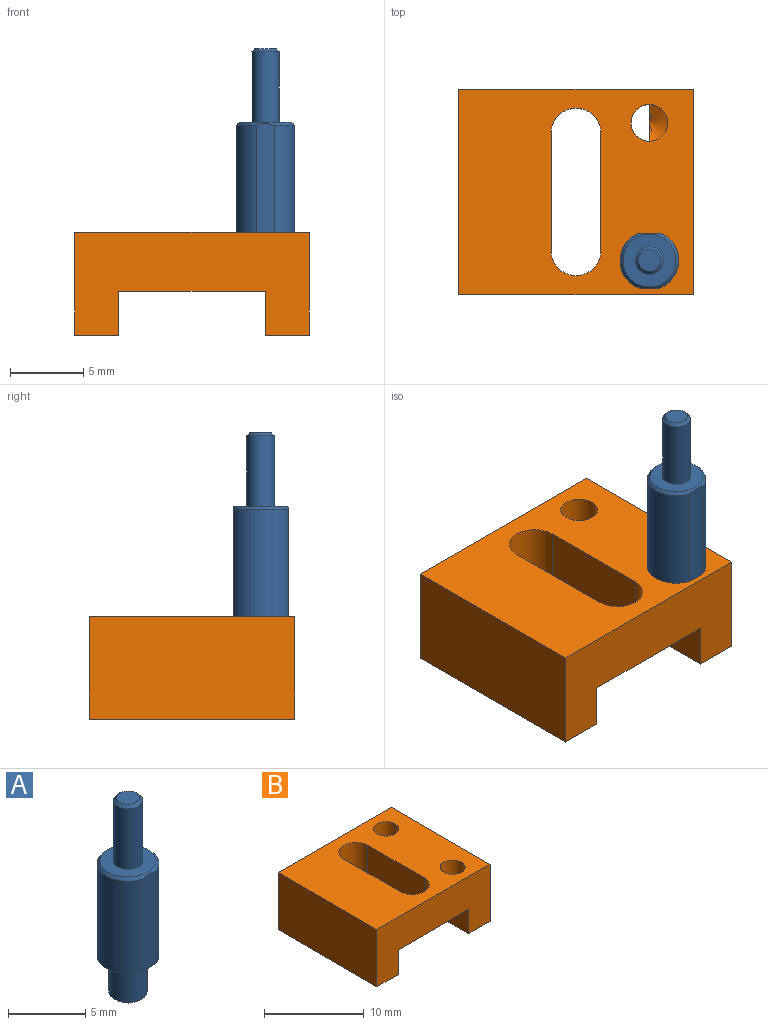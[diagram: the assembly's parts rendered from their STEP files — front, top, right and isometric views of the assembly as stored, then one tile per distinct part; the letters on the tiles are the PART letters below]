
ASSEMBLY  parts=2 mates=1
PART A: 13 faces, bbox 4x4x15.5 mm
  f0: cylinder r=2mm len=7.3mm, axis (0,0,-1), area 35.5mm2, adj f2,f3,f11,f12
  f1: cylinder r=2mm len=7.3mm, axis (0,0,-1), area 35.5mm2, adj f2,f3,f11,f12
  f2: plane 4x3.75mm, normal (0,0,-1), area 7.4mm2, adj f0,f1,f5,f11,f12
  f3: cone r=1.8mm half-angle=45deg, axis (0,0,-1), area 3mm2, adj f0,f1,f4,f11,f12
  f4: plane 3.6x3.6mm, normal (0,0,1), area 7.3mm2, adj f3,f7
  f5: cylinder r=1.25mm len=2.8mm, axis (0,0,1), area 22mm2, adj f2,f10
  f6: plane 2.1x2.1mm, normal (0,0,-1), area 3.5mm2, adj f10
  f7: cylinder r=0.95mm len=4.8mm, axis (0,0,-1), area 28.7mm2, adj f4,f9
  f8: plane 1.5x1.5mm, normal (0,0,1), area 1.8mm2, adj f9
  f9: cone r=0.75mm half-angle=45deg, axis (0,0,-1), area 1.5mm2, adj f7,f8
  f10: cone r=1.25mm half-angle=45deg, axis (0,0,1), area 2mm2, adj f5,f6
  f11: plane 7.4x1.25mm, normal (0,-1,0), area 9.2mm2, adj f0,f1,f2,f3
  f12: plane 7.45x1.52mm, normal (0,1,0), area 11.2mm2, adj f0,f1,f2,f3
PART B: 18 faces, bbox 16x14x7 mm
  f0: plane 14x3mm, normal (-1,0,0), area 40.1mm2, adj f6,f7,f8,f9,f10,f12
  f1: plane 14x3mm, normal (1,0,0), area 42mm2, adj f2,f7,f8,f9
  f2: plane 14x3mm, normal (0,0,-1), area 42mm2, adj f1,f3,f8,f9
  f3: plane 14x7mm, normal (-1,0,0), area 98mm2, adj f2,f4,f8,f9
  f4: plane 16x14mm, normal (0,0,1), area 177.9mm2, adj f3,f5,f8,f9,f11,f13,f14,f15
  f5: plane 14x7mm, normal (1,0,0), area 98mm2, adj f4,f6,f8,f9
  f6: plane 14x3mm, normal (0,0,-1), area 42mm2, adj f0,f5,f8,f9
  f7: plane 14x10mm, normal (0,0,-1), area 98.8mm2, adj f0,f1,f8,f9,f11,f13,f14,f15
  f8: plane 16x7mm, normal (0,1,0), area 82mm2, adj f0,f1,f2,f3,f4,f5,f6,f7
  f9: plane 16x7mm, normal (0,-1,0), area 82mm2, adj f0,f1,f2,f3,f4,f5,f6,f7
  f10: cone r=0mm half-angle=59deg, axis (0,0,1), area 2.9mm2, adj f0,f11
  f11: cylinder r=1.25mm len=4mm, axis (0,0,1), area 31.4mm2, adj f4,f7,f10
  f12: cone r=0mm half-angle=59deg, axis (0,0,1), area 2.9mm2, adj f0,f13
  f13: cylinder r=1.25mm len=4mm, axis (0,0,1), area 31.4mm2, adj f4,f7,f12
  f14: plane 8x4mm, normal (1,0,0), area 32mm2, adj f4,f7,f15,f17
  f15: cylinder r=1.7mm len=4mm, axis (0,0,1), area 21.4mm2, adj f4,f7,f14,f16
  f16: plane 8x4mm, normal (-1,0,0), area 32mm2, adj f4,f7,f15,f17
  f17: cylinder r=1.7mm len=4mm, axis (0,0,1), area 21.4mm2, adj f4,f7,f14,f16
PLACE A t=(34.58,-39.17,-10)mm
PLACE B t=(34.58,-29.78,-10)mm
MATE fastened A.f2 <-> B.f10  axis (0,0,-1) through (154.52,24.78,7.5)mm
